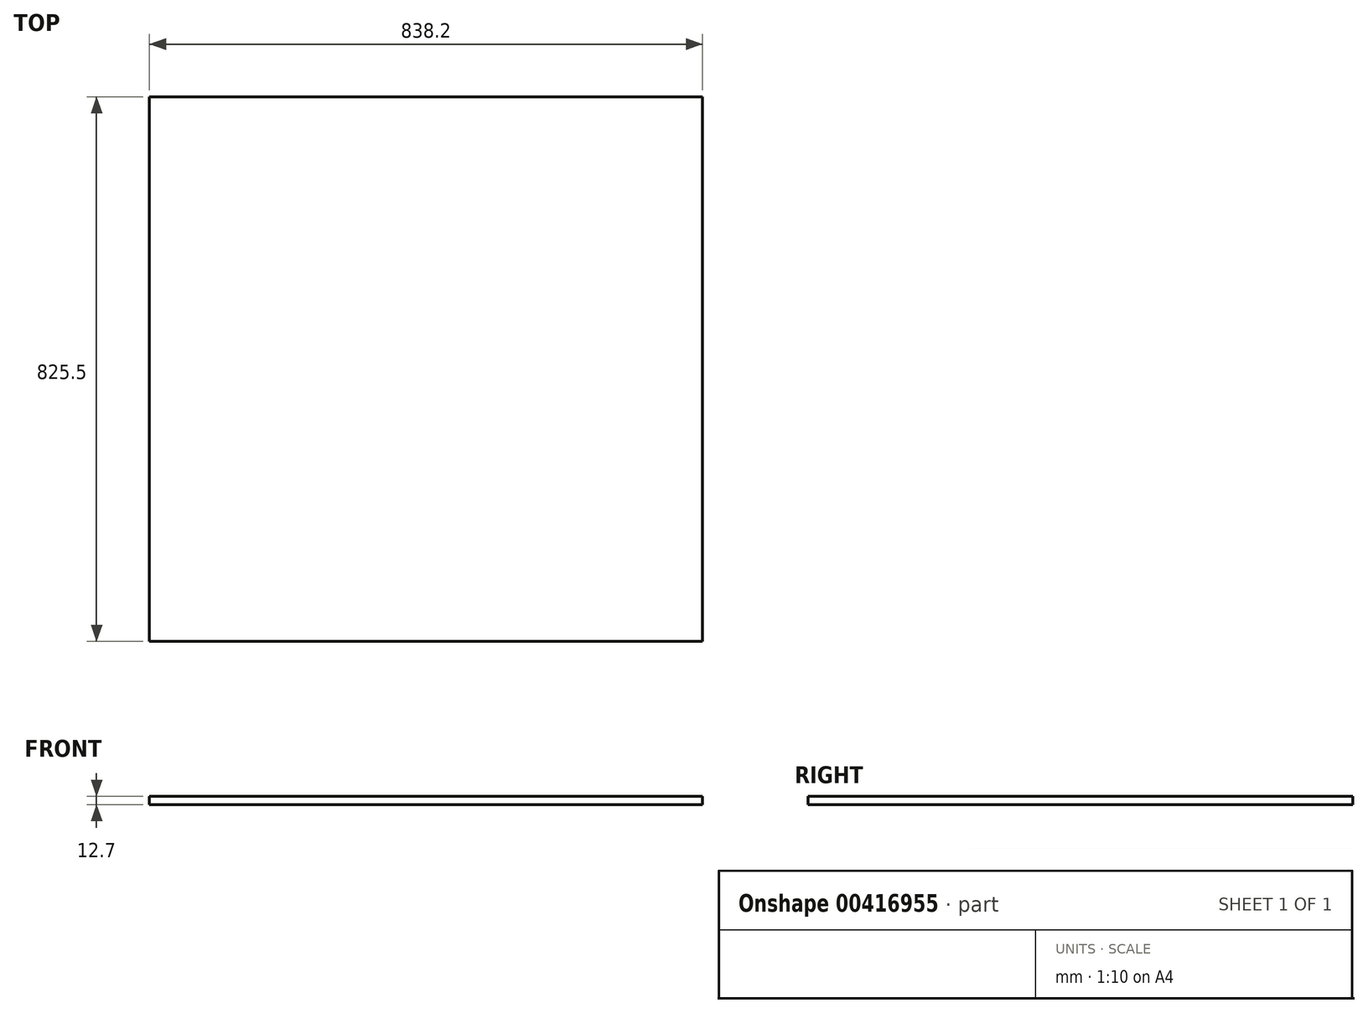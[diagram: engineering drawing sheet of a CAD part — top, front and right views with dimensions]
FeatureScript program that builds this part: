
annotation { "Feature Type Name" : "Feature", "Feature Type Description" : "" }
export const myFeature = defineFeature(function(context is Context, id is Id, definition is map)
    precondition{}
    {
        {
            var Q0;
            Q0=qCreatedBy(makeId("Top.planeOp"),FACE);
            var sketch = newSketch(context, id + "F0", { "sketchPlane" : qUnion([Q0])});
            skLineSegment(sketch, "E0.bottom", {"start": v(419.1, 412.75) * mm, "end": v(-419.1, 412.75) * mm});
            skLineSegment(sketch, "E0.top", {"start": v(419.1, -412.75) * mm, "end": v(-419.1, -412.75) * mm});
            skLineSegment(sketch, "E0.left", {"start": v(419.1, 412.75) * mm, "end": v(419.1, -412.75) * mm});
            skLineSegment(sketch, "E0.right", {"start": v(-419.1, 412.75) * mm, "end": v(-419.1, -412.75) * mm});
            skPoint(sketch, "E0.middle", {"position": v(0, 0) * mm});
            skSolve(sketch);
        }
        {
            var Q0;
            Q0 = qSketchRegion(id + "F0", true);
            extrude(context, id + "F1", {"entities" : qUnion([Q0]), "depth" : 12.7 * mm});
        }
    });
